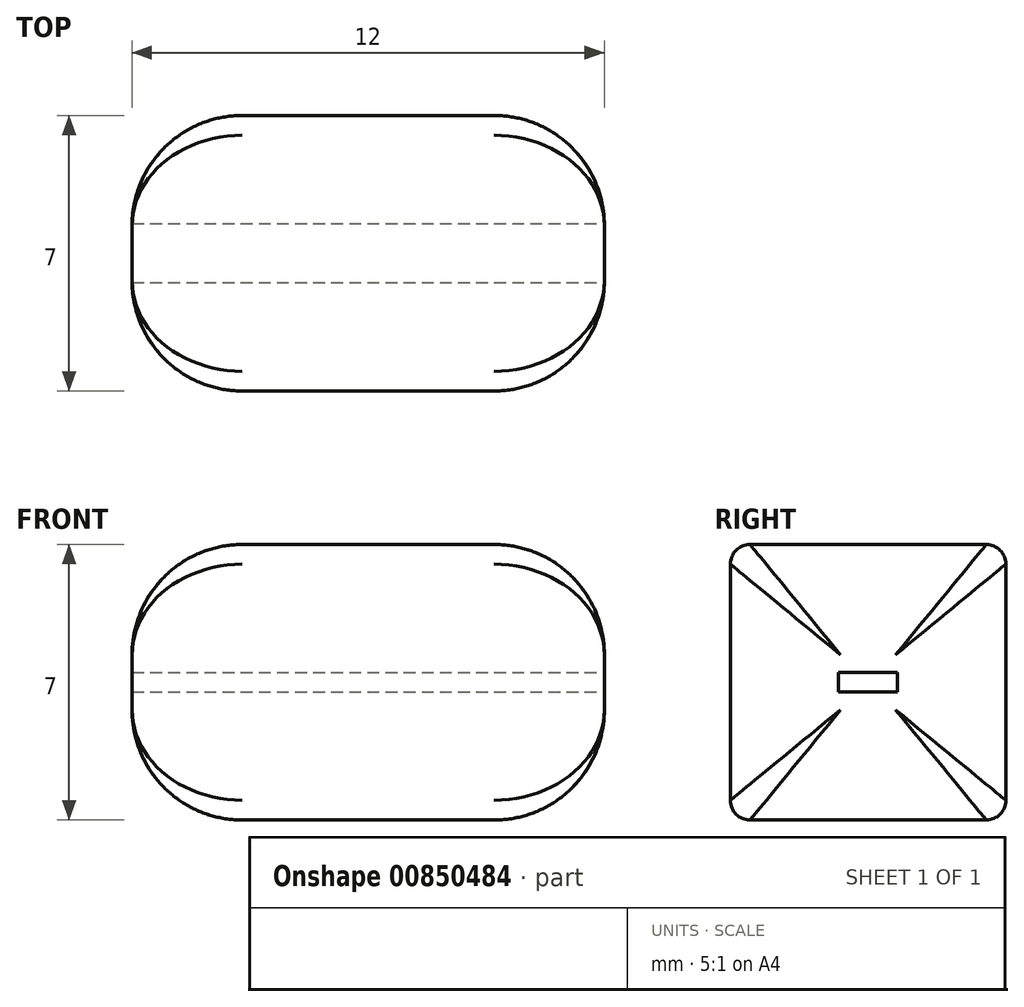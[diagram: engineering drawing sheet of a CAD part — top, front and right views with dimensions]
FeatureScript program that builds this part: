
annotation { "Feature Type Name" : "Feature", "Feature Type Description" : "" }
export const myFeature = defineFeature(function(context is Context, id is Id, definition is map)
    precondition{}
    {
        {
            var Q0;
            Q0=qCreatedBy(makeId("Front.planeOp"),FACE);
            var sketch = newSketch(context, id + "F0", { "sketchPlane" : qUnion([Q0])});
            skLineSegment(sketch, "E0.bottom", {"start": v(6, 3.5) * mm, "end": v(-6, 3.5) * mm});
            skLineSegment(sketch, "E0.top", {"start": v(6, -3.5) * mm, "end": v(-6, -3.5) * mm});
            skLineSegment(sketch, "E0.left", {"start": v(6, 3.5) * mm, "end": v(6, -3.5) * mm});
            skLineSegment(sketch, "E0.right", {"start": v(-6, 3.5) * mm, "end": v(-6, -3.5) * mm});
            skPoint(sketch, "E0.middle", {"position": v(0, 0) * mm});
            skSolve(sketch);
        }
        {
            var Q0;
            Q0=makeQuery(id+"F0.imprint","IMPRINT",FACE,{"disambiguationData":[TD([[makeQuery(id+"F0.imprint","IMPRINT",EDGE,{"derivedFrom":sQuery(id+"F0.wireOp",EDGE,"E0.bottom")}),1.0]])]});
            extrude(context, id + "F1", {"entities" : qUnion([Q0]), "endBound" : BoundingType.SYMMETRIC, "depth" : 7 * mm, "offsetDistance" : 25 * mm});
        }
        {
            var Q0;
            Q0=makeQuery(id+"F1.opExtrude","SWEPT_FACE",FACE,{"disambiguationData":[OSD([sQuery(id+"F0.wireOp",EDGE,"E0.left")])]});
            var sketch = newSketch(context, id + "F2", { "sketchPlane" : qUnion([Q0])});
            skLineSegment(sketch, "E1.bottom", {"start": v(0.75, 0.25) * mm, "end": v(-0.75, 0.25) * mm});
            skLineSegment(sketch, "E1.top", {"start": v(0.75, -0.25) * mm, "end": v(-0.75, -0.25) * mm});
            skLineSegment(sketch, "E1.left", {"start": v(0.75, 0.25) * mm, "end": v(0.75, -0.25) * mm});
            skLineSegment(sketch, "E1.right", {"start": v(-0.75, 0.25) * mm, "end": v(-0.75, -0.25) * mm});
            skPoint(sketch, "E1.middle", {"position": v(0, 0) * mm});
            skSolve(sketch);
        }
        {
            var Q0;
            Q0=makeQuery(id+"F2.imprint","IMPRINT",FACE,{"disambiguationData":[TD([[makeQuery(id+"F2.imprint","IMPRINT",EDGE,{"derivedFrom":sQuery(id+"F2.wireOp",EDGE,"E1.bottom")}),1.0]])]});
            extrude(context, id + "F3", {"entities" : qUnion([Q0]), "operationType" : NewBodyOperationType.REMOVE, "oppositeDirection" : true, "depth" : 12 * mm, "offsetDistance" : 25 * mm});
        }
        {
            var Q0;
            Q0=makeQuery(id+"F1.opExtrude","CAP_EDGE",EDGE,{"disambiguationData":[OSD([sQuery(id+"F0.wireOp",EDGE,"E0.bottom")])],"isStart":false});
            var Q1;
            Q1=makeQuery(id+"F1.opExtrude","CAP_EDGE",EDGE,{"disambiguationData":[OSD([sQuery(id+"F0.wireOp",EDGE,"E0.bottom")])],"isStart":true});
            var Q2;
            Q2=makeQuery(id+"F1.opExtrude","CAP_EDGE",EDGE,{"disambiguationData":[OSD([sQuery(id+"F0.wireOp",EDGE,"E0.top")])],"isStart":false});
            var Q3;
            Q3=makeQuery(id+"F1.opExtrude","CAP_EDGE",EDGE,{"disambiguationData":[OSD([sQuery(id+"F0.wireOp",EDGE,"E0.top")])],"isStart":true});
            fillet(context, id + "F4", {"entities" : qUnion([Q0, Q1, Q2, Q3]), "radius" : 0.5 * mm, "tangentPropagation" : true, "allowEdgeOverflow" : false});
        }
        {
            var Q0;
            Q0=makeQuery(id+"F1.opExtrude","SWEPT_EDGE",EDGE,{"disambiguationData":[OSD([sQuery(id+"F0.wireOp",EDGE,"E0.bottom"),sQuery(id+"F0.wireOp",EDGE,"E0.left")])]});
            var Q1;
            Q1=makeQuery(id+"F1.opExtrude","SWEPT_EDGE",EDGE,{"disambiguationData":[OSD([sQuery(id+"F0.wireOp",EDGE,"E0.top"),sQuery(id+"F0.wireOp",EDGE,"E0.left")])]});
            var Q2;
            Q2=makeQuery(id+"F1.opExtrude","SWEPT_EDGE",EDGE,{"disambiguationData":[OSD([sQuery(id+"F0.wireOp",EDGE,"E0.bottom"),sQuery(id+"F0.wireOp",EDGE,"E0.right")])]});
            fillet(context, id + "F5", {"entities" : qUnion([Q0, Q1, Q2]), "radius" : 2.8 * mm, "tangentPropagation" : true, "allowEdgeOverflow" : false});
        }
    });
